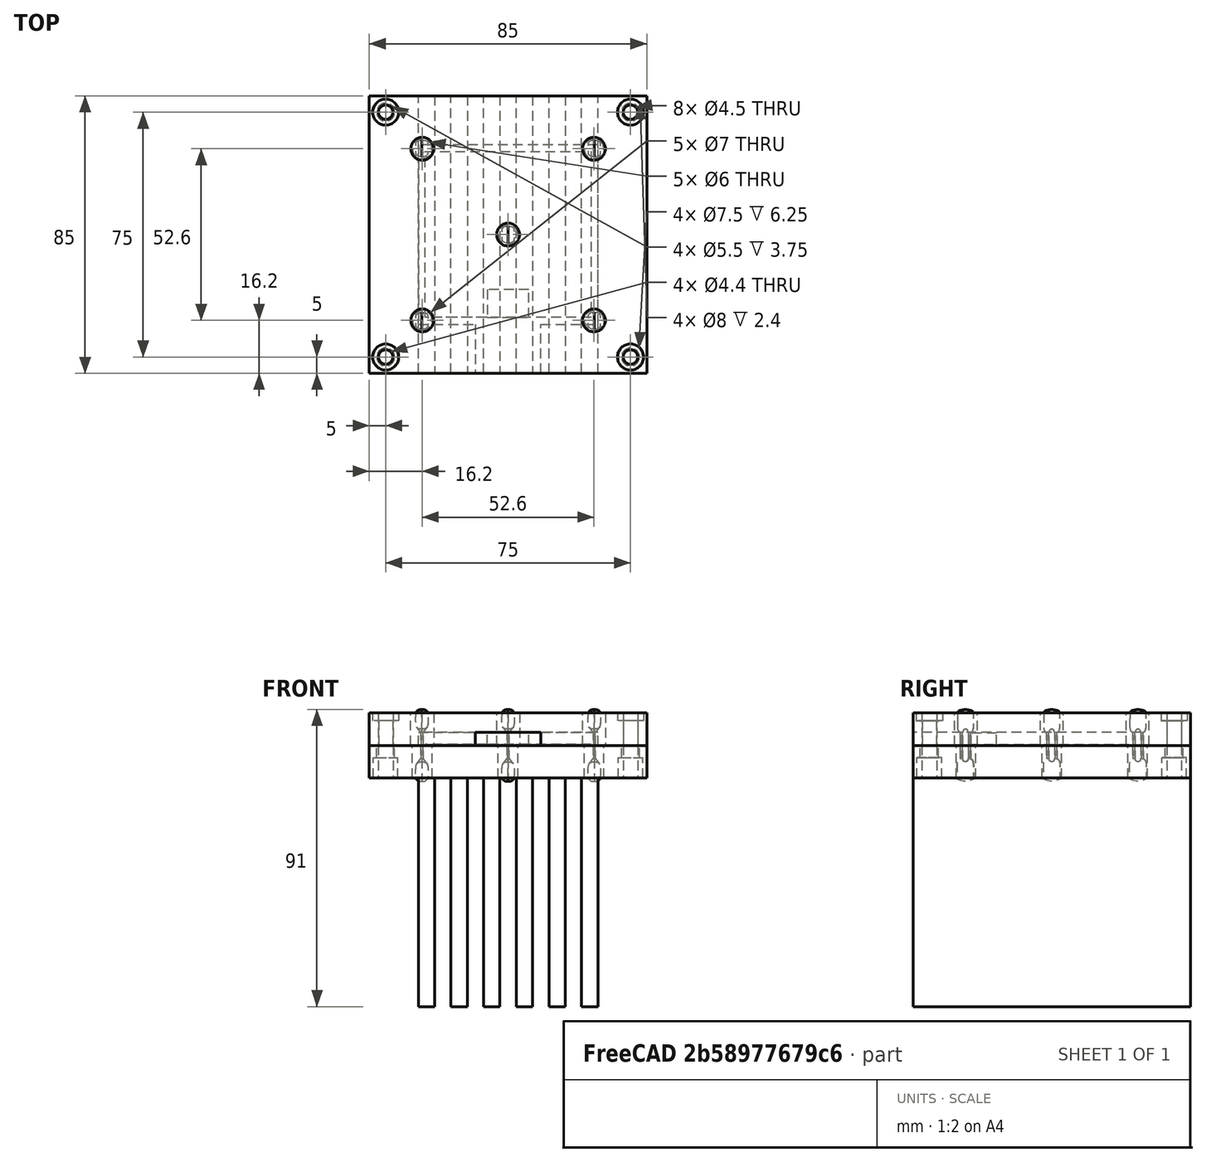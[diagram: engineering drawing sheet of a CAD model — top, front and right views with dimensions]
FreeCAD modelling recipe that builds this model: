
FCSTD DOCUMENT  (FreeCAD 0.18R4 (GitTag))
Label: thermal_cond_tester
License: All rights reserved
LicenseURL: http://en.wikipedia.org/wiki/All_rights_reserved
objects: PartDesign::Body×16, Sketcher::SketchObject×15, PartDesign::FeatureBase×11, PartDesign::Pad×6, PartDesign::Pocket×6, PartDesign::Hole×5, PartDesign::Mirrored×2, App::DocumentObjectGroup×2, App::Part×2, Part::Feature×1, Spreadsheet::Sheet×1, Fem::FemSolverObjectPython×1
note: 79 computed .brp shape members not serialized (recipe doc carries the construction recipe); baked Part::Feature solids carry a one-line shape summary decoded from their .brp

FEATURE [Sketcher::SketchObject] Sketch
  MapMode = 5
  Support = -> [XY_Plane003]
  sketch-geometry (4):
    g0: LineSegment StartX=-42.5 StartY=42.5 StartZ=0 EndX=42.5 EndY=42.5 EndZ=0
    g1: LineSegment StartX=42.5 StartY=42.5 StartZ=0 EndX=42.5 EndY=-42.5 EndZ=0
    g2: LineSegment StartX=42.5 StartY=-42.5 StartZ=0 EndX=-42.5 EndY=-42.5 EndZ=0
    g3: LineSegment StartX=-42.5 StartY=-42.5 StartZ=0 EndX=-42.5 EndY=42.5 EndZ=0
  constraints (12):
    c: Coincident(g0,g1)
    c: Coincident(g1,g2)
    c: Coincident(g2,g3)
    c: Coincident(g3,g0)
    c: Horizontal(g0)
    c: Horizontal(g2)
    c: Vertical(g1)
    c: Vertical(g3)
    c: DistanceX(g0,g0) = 85
    c: DistanceY(g1,g1) = 85
    c: DistanceX(g2,g-1) = 42.5
    c: DistanceY(g2,g-1) = 42.5
FEATURE [Sketcher::SketchObject] Sketch003
  MapMode = 2
  sketch-geometry (4):
    g0: LineSegment StartX=-25.4 StartY=25.4 StartZ=0 EndX=25.4 EndY=25.4 EndZ=0
    g1: LineSegment StartX=25.4 StartY=25.4 StartZ=0 EndX=25.4 EndY=-25.4 EndZ=0
    g2: LineSegment StartX=25.4 StartY=-25.4 StartZ=0 EndX=-25.4 EndY=-25.4 EndZ=0
    g3: LineSegment StartX=-25.4 StartY=-25.4 StartZ=0 EndX=-25.4 EndY=25.4 EndZ=0
  constraints (10):
    c: Coincident(g0,g1)
    c: Coincident(g1,g2)
    c: Coincident(g2,g3)
    c: Coincident(g3,g0)
    c: Horizontal(g2)
    c: Vertical(g1)
    c: Symmetric(g0,g0,g-2)
    c: Symmetric(g2,g0,g-1)
    c: DistanceX(g0,g0) = 50.8
    c: DistanceY(g1,g1) = 50.8
FEATURE [PartDesign::Pad] Pad001
  Length = 0.3
  Length2 = 100
  Profile = -> Sketch003
  Type = 0
FEATURE [Sketcher::SketchObject] Sketch004
  ExternalGeometry = -> [Pad001]
  MapMode = 5
  Placement = pos=(0,0,0.3) rot=(0,0,1;0rad)
  Support = -> [Pad001]
  sketch-geometry (4):
    g0: LineSegment StartX=6.35 StartY=-16.9 StartZ=0 EndX=-6.35 EndY=-16.9 EndZ=0
    g1: LineSegment StartX=-6.35 StartY=-16.9 StartZ=0 EndX=-6.35 EndY=-25.4 EndZ=0
    g2: LineSegment StartX=-6.35 StartY=-25.4 StartZ=0 EndX=6.35 EndY=-25.4 EndZ=0
    g3: LineSegment StartX=6.35 StartY=-25.4 StartZ=0 EndX=6.35 EndY=-16.9 EndZ=0
  constraints (11):
    c: Coincident(g0,g1)
    c: Coincident(g1,g2)
    c: Coincident(g2,g3)
    c: Coincident(g3,g0)
    c: Horizontal(g2)
    c: Vertical(g1)
    c: Vertical(g3)
    c: PointOnObject(g2,g-3)
    c: Symmetric(g0,g0,g-2)
    c: DistanceX(g0,g0) = 12.7
    c: DistanceY(g1,g1) = 8.5
FEATURE [PartDesign::Pad] Pad002
  BaseFeature = -> Pad001
  Length = 3.51
  Length2 = 100
  Profile = -> Sketch004
  Type = 0
FEATURE [PartDesign::Body] Body001  label="Heater Foil"
  Group = -> [Sketch003,Pad001,Sketch004,Pad002]
  Origin = -> Origin001
  Tip = -> Pad002
FEATURE [PartDesign::Pad] Pad
  Length = 10
  Length2 = 100
  Profile = -> Sketch
  Type = 0
FEATURE [Sketcher::SketchObject] Sketch002
  ExternalGeometry = -> [Pad]
  MapMode = 5
  Placement = pos=(0,0,10) rot=(0,0,1;0rad)
  Support = -> [Pad]
  sketch-geometry (4):
    g0: Circle CenterX=-37.5 CenterY=37.5 CenterZ=0 NormalX=0 NormalY=0 NormalZ=1 AngleXU=0 Radius=2
    g1: Circle CenterX=37.5 CenterY=37.5 CenterZ=0 NormalX=0 NormalY=0 NormalZ=1 AngleXU=0 Radius=2
    g2: Circle CenterX=37.5 CenterY=-37.5 CenterZ=0 NormalX=0 NormalY=0 NormalZ=1 AngleXU=0 Radius=2
    g3: Circle CenterX=-37.5 CenterY=-37.5 CenterZ=0 NormalX=0 NormalY=0 NormalZ=1 AngleXU=0 Radius=2
  constraints (9):
    c: Symmetric(g1,g0,g-2)
    c: Symmetric(g2,g1,g-1)
    c: Symmetric(g0,g3,g-1)
    c: DistanceX(g-3,g0) = 5
    c: DistanceY(g0,g-3) = 5
    c: Radius(g0) = 2
    c: Equal(g0,g1)
    c: Equal(g1,g2)
    c: Equal(g2,g3)
FEATURE [PartDesign::Hole] Hole
  BaseFeature = -> Pad
  Depth = 25
  DepthType = 0
  Diameter = 4.4
  DrillPoint = 1
  DrillPointAngle = 118
  HoleCutCountersinkAngle = 90
  HoleCutDepth = 2.4
  HoleCutDiameter = 8
  HoleCutType = 1
  ModelActualThread = false
  Profile = -> Sketch002
  Tapered = false
  TaperedAngle = 90
  ThreadAngle = 60
  ThreadClass = 0
  ThreadCutOffInner = 0.0541266
  ThreadCutOffOuter = 0.108253
  ThreadDirection = 0
  ThreadFit = 0
  ThreadPitch = 0.5
  ThreadSize = 11
  ThreadType = 2
  Threaded = false
FEATURE [Sketcher::SketchObject] Sketch001
  MapMode = 5
  Placement = pos=(0,0,0) rot=(1,0,0;3.14159rad)
  Support = -> [Pad]
  sketch-geometry (4):
    g0: LineSegment StartX=-27.5 StartY=27.5 StartZ=0 EndX=27.5 EndY=27.5 EndZ=0
    g1: LineSegment StartX=27.5 StartY=27.5 StartZ=0 EndX=27.5 EndY=-27.5 EndZ=0
    g2: LineSegment StartX=27.5 StartY=-27.5 StartZ=0 EndX=-27.5 EndY=-27.5 EndZ=0
    g3: LineSegment StartX=-27.5 StartY=-27.5 StartZ=0 EndX=-27.5 EndY=27.5 EndZ=0
  constraints (10):
    c: Coincident(g0,g1)
    c: Coincident(g1,g2)
    c: Coincident(g2,g3)
    c: Coincident(g3,g0)
    c: Horizontal(g2)
    c: Vertical(g3)
    c: Symmetric(g0,g0,g-2)
    c: Symmetric(g1,g0,g-1)
    c: DistanceX(g0,g0) = 55
    c: Equal(g1,g0)
FEATURE [PartDesign::Pocket] Pocket
  BaseFeature = -> Hole
  Length = 4
  Length2 = 100
  Profile = -> Sketch001
  Type = 0
FEATURE [PartDesign::Pad] Pad003
  Length = 10
  Length2 = 100
  Profile = -> Sketch
  Type = 0
FEATURE [Sketcher::SketchObject] Sketch005
  ExternalGeometry = -> [Pad]
  MapMode = 5
  Placement = pos=(0,0,10) rot=(0,0,1;0rad)
  Support = -> [Pad]
  sketch-geometry (4):
    g0: Circle CenterX=-37.5 CenterY=37.5 CenterZ=0 NormalX=0 NormalY=0 NormalZ=1 AngleXU=0 Radius=2
    g1: Circle CenterX=37.5 CenterY=37.5 CenterZ=0 NormalX=0 NormalY=0 NormalZ=1 AngleXU=0 Radius=2
    g2: Circle CenterX=37.5 CenterY=-37.5 CenterZ=0 NormalX=0 NormalY=0 NormalZ=1 AngleXU=0 Radius=2
    g3: Circle CenterX=-37.5 CenterY=-37.5 CenterZ=0 NormalX=0 NormalY=0 NormalZ=1 AngleXU=0 Radius=2
  constraints (9):
    c: Symmetric(g1,g0,g-2)
    c: Symmetric(g2,g1,g-1)
    c: Symmetric(g0,g3,g-1)
    c: DistanceX(g-3,g0) = 5
    c: DistanceY(g0,g-3) = 5
    c: Radius(g0) = 2
    c: Equal(g0,g1)
    c: Equal(g1,g2)
    c: Equal(g2,g3)
FEATURE [PartDesign::Hole] Hole001
  BaseFeature = -> Pad003
  Depth = 25
  DepthType = 0
  Diameter = 4.5
  DrillPoint = 1
  DrillPointAngle = 118
  HoleCutCountersinkAngle = 90
  HoleCutDepth = 0
  HoleCutDiameter = 5
  HoleCutType = 0
  ModelActualThread = false
  Profile = -> Sketch005
  Tapered = false
  TaperedAngle = 90
  ThreadAngle = 60
  ThreadClass = 0
  ThreadCutOffInner = 0.0541266
  ThreadCutOffOuter = 0.108253
  ThreadDirection = 1
  ThreadFit = 0
  ThreadPitch = 0.5
  ThreadSize = 13
  ThreadType = 2
  Threaded = true
FEATURE [Part::Feature] Part__Feature  label="Thermister Ref"
  Placement = pos=(26.3,26.3,-4) rot=(0,1,0;1.5708rad)
  shape: bbox 4.003 x 5.103 x 24 mm, 8 faces (baked)
FEATURE [Sketcher::SketchObject] Sketch006
  MapMode = 5
  Placement = pos=(0,0,0) rot=(1,0,0;3.14159rad)
  Support = -> [Hole001]
  sketch-geometry (5):
    g0: Circle CenterX=0 CenterY=0 CenterZ=0 NormalX=0 NormalY=0 NormalZ=1 AngleXU=0 Radius=3.5
    g1: Circle CenterX=-26.3 CenterY=26.3 CenterZ=0 NormalX=0 NormalY=0 NormalZ=1 AngleXU=0 Radius=3.5
    g2: Circle CenterX=26.3 CenterY=26.3 CenterZ=0 NormalX=0 NormalY=0 NormalZ=1 AngleXU=0 Radius=3.5
    g3: Circle CenterX=26.3 CenterY=-26.3 CenterZ=0 NormalX=0 NormalY=0 NormalZ=1 AngleXU=0 Radius=3.5
    g4: Circle CenterX=-26.3 CenterY=-26.3 CenterZ=0 NormalX=0 NormalY=0 NormalZ=1 AngleXU=0 Radius=3.5
  constraints (11):
    c: Diameter(g0) = 7
    c: Coincident(g0,g-1)
    c: Equal(g4,g1)
    c: Equal(g1,g0)
    c: Equal(g0,g2)
    c: Equal(g2,g3)
    c: Symmetric(g1,g2,g-2)
    c: Symmetric(g2,g3,g-1)
    c: Symmetric(g4,g1,g-1)
    c: DistanceX(g1,g-1) = 26.3
    c: DistanceY(g-1,g1) = 26.3
FEATURE [PartDesign::Hole] Hole002
  BaseFeature = -> Hole001
  Depth = 25
  DepthType = 0
  Diameter = 6
  DrillPoint = 1
  DrillPointAngle = 118
  HoleCutCountersinkAngle = 90
  HoleCutDepth = 0
  HoleCutDiameter = 0
  HoleCutType = 0
  ModelActualThread = false
  Profile = -> Sketch006
  Tapered = false
  TaperedAngle = 90
  ThreadAngle = 0
  ThreadClass = 0
  ThreadCutOffInner = 0
  ThreadCutOffOuter = 0
  ThreadDirection = 0
  ThreadFit = 0
  ThreadPitch = 0
  ThreadSize = 0
  ThreadType = 0
  Threaded = false
FEATURE [PartDesign::Body] Body002  label="Hot Plate Bottom"
  Group = -> [Pad003,Sketch005,Hole001,Sketch006,Hole002]
  Origin = -> Origin003
  Placement = pos=(0,0,-10) rot=(0,0,1;0rad)
  Tip = -> Hole002
FEATURE [Spreadsheet::Sheet] Spreadsheet
  cells = B3=Part Desc; C3=URL; B4=Thermistor; C4=https://www.digikey.com/product-detail/en/vishay-bc-components/NTCLE100E3103JB0/BC2301-ND/769411; B5=Heater; C5=http://catalog.minco.com/catalog3/d/minco/?c=products&cid=3_1-polyimide-thermofoil-heaters&id=HK6911
FEATURE [PartDesign::FeatureBase] BaseFeature
  BaseFeature = -> Part__Feature
FEATURE [PartDesign::Pocket] Pocket001
  BaseFeature = -> BaseFeature
  Length = 10
  Length2 = 100
  Profile = -> BaseFeature [Face6]
  Type = 0
FEATURE [PartDesign::Mirrored] Mirrored
  BaseFeature = -> Pocket001
  MirrorPlane = -> XZ_Plane004
  Originals = -> [Pocket001]
FEATURE [PartDesign::Body] Body003  label="Shortened Thermister"
  BaseFeature = -> Part__Feature
  Group = -> [BaseFeature,Pocket001,Mirrored]
  Origin = -> Origin004
  Tip = -> Mirrored
FEATURE [PartDesign::FeatureBase] Clone
  BaseFeature = -> Body003
FEATURE [PartDesign::Body] Body004  label="Thermister 1"
  BaseFeature = -> Body003
  Group = -> [Clone]
  Origin = -> Origin005
  Placement = pos=(0,0,-4) rot=(0,1,0;1.5708rad)
  Tip = -> Clone
FEATURE [PartDesign::FeatureBase] Clone001
  BaseFeature = -> Body003
FEATURE [PartDesign::Body] Body005  label="Thermister 2"
  BaseFeature = -> Body003
  Group = -> [Clone001]
  Origin = -> Origin006
  Placement = pos=(26.4,26.4,-4) rot=(0,1,0;1.5708rad)
  Tip = -> Clone001
FEATURE [PartDesign::FeatureBase] Clone002
  BaseFeature = -> Body003
FEATURE [PartDesign::Body] Body006  label="Thermister 3"
  BaseFeature = -> Body003
  Group = -> [Clone002]
  Origin = -> Origin007
  Placement = pos=(26.4,-26.4,-4) rot=(0,1,0;1.5708rad)
  Tip = -> Clone002
FEATURE [PartDesign::FeatureBase] Clone003
  BaseFeature = -> Body003
FEATURE [PartDesign::Body] Body007  label="Thermister 4"
  BaseFeature = -> Body003
  Group = -> [Clone003]
  Origin = -> Origin008
  Placement = pos=(-26.4,26.4,-4) rot=(0,1,0;1.5708rad)
  Tip = -> Clone003
FEATURE [PartDesign::FeatureBase] Clone004
  BaseFeature = -> Body003
FEATURE [PartDesign::Body] Body008  label="Thermister 5"
  BaseFeature = -> Body003
  Group = -> [Clone004]
  Origin = -> Origin009
  Placement = pos=(-26.4,-26.5,-4) rot=(0,1,0;1.5708rad)
  Tip = -> Clone004
FEATURE [App::DocumentObjectGroup] Group  label="Reference Parts"
  Group = -> [Part__Feature,Body003]
FEATURE [App::DocumentObjectGroup] Group001  label="Documentation"
  Group = -> [Spreadsheet]
FEATURE [Sketcher::SketchObject] Sketch007
  ExternalGeometry = -> [Pocket]
  MapMode = 5
  Placement = pos=(0,0,0) rot=(1,0,0;3.14159rad)
  Support = -> [Pocket]
  sketch-geometry (4):
    g0: LineSegment StartX=-10 StartY=42.5 StartZ=0 EndX=10 EndY=42.5 EndZ=0
    g1: LineSegment StartX=10 StartY=42.5 StartZ=0 EndX=10 EndY=27.5 EndZ=0
    g2: LineSegment StartX=10 StartY=27.5 StartZ=0 EndX=-10 EndY=27.5 EndZ=0
    g3: LineSegment StartX=-10 StartY=27.5 StartZ=0 EndX=-10 EndY=42.5 EndZ=0
  constraints (11):
    c: Coincident(g0,g1)
    c: Coincident(g1,g2)
    c: Coincident(g2,g3)
    c: Coincident(g3,g0)
    c: Horizontal(g0)
    c: Vertical(g1)
    c: Vertical(g3)
    c: PointOnObject(g0,g-3)
    c: PointOnObject(g2,g-4)
    c: Symmetric(g2,g1,g-2)
    c: DistanceX(g2,g2) = 20
FEATURE [PartDesign::Pocket] Pocket002
  BaseFeature = -> Pocket
  Length = 4
  Length2 = 100
  Profile = -> Sketch007
  Type = 0
FEATURE [PartDesign::Body] Body  label="Hot Plate Top"
  Group = -> [Sketch,Pad,Sketch001,Sketch002,Hole,Pocket,Sketch007,Pocket002]
  Origin = -> Origin
  Tip = -> Pocket002
FEATURE [App::Part] Part  label="Hot Side"
  Group = -> [Body001,Body,Body002,Body004,Body005,Body006,Body007,Body008]
  Origin = -> Origin002
FEATURE [Sketcher::SketchObject] Sketch008
  MapMode = 5
  Support = -> [XY_Plane011]
  sketch-geometry (4):
    g0: LineSegment StartX=-42.5 StartY=42.5 StartZ=0 EndX=42.5 EndY=42.5 EndZ=0
    g1: LineSegment StartX=42.5 StartY=42.5 StartZ=0 EndX=42.5 EndY=-42.5 EndZ=0
    g2: LineSegment StartX=42.5 StartY=-42.5 StartZ=0 EndX=-42.5 EndY=-42.5 EndZ=0
    g3: LineSegment StartX=-42.5 StartY=-42.5 StartZ=0 EndX=-42.5 EndY=42.5 EndZ=0
  constraints (10):
    c: Coincident(g0,g1)
    c: Coincident(g1,g2)
    c: Coincident(g2,g3)
    c: Coincident(g3,g0)
    c: Horizontal(g2)
    c: Vertical(g3)
    c: DistanceX(g0,g0) = 85
    c: Symmetric(g0,g0,g-2)
    c: Equal(g1,g0)
    c: Symmetric(g1,g0,g-1)
FEATURE [PartDesign::Pad] Pad004
  Length = 10
  Length2 = 100
  Profile = -> Sketch008
  Type = 0
FEATURE [Sketcher::SketchObject] Sketch009
  ExternalGeometry = -> [Pad004]
  MapMode = 5
  Placement = pos=(0,0,10) rot=(0,0,1;0rad)
  Support = -> [Pad004]
  sketch-geometry (4):
    g0: Circle CenterX=-37.5 CenterY=37.5 CenterZ=0 NormalX=0 NormalY=0 NormalZ=1 AngleXU=0 Radius=2
    g1: Circle CenterX=37.5 CenterY=37.5 CenterZ=0 NormalX=0 NormalY=0 NormalZ=1 AngleXU=0 Radius=2
    g2: Circle CenterX=37.5 CenterY=-37.5 CenterZ=0 NormalX=0 NormalY=0 NormalZ=1 AngleXU=0 Radius=2
    g3: Circle CenterX=-37.5 CenterY=-37.5 CenterZ=0 NormalX=0 NormalY=0 NormalZ=1 AngleXU=0 Radius=2
  constraints (9):
    c: Radius(g0) = 2
    c: DistanceX(g-3,g0) = 5
    c: DistanceY(g0,g-3) = 5
    c: Equal(g0,g1)
    c: Equal(g1,g2)
    c: Equal(g2,g3)
    c: Symmetric(g0,g1,g-2)
    c: Symmetric(g3,g2,g-2)
    c: Symmetric(g0,g3,g-1)
FEATURE [PartDesign::Hole] Hole003
  BaseFeature = -> Pad004
  Depth = 25
  DepthType = 0
  Diameter = 4.5
  DrillPoint = 1
  DrillPointAngle = 118
  HoleCutCountersinkAngle = 90
  HoleCutDepth = 0
  HoleCutDiameter = 5
  HoleCutType = 0
  ModelActualThread = false
  Profile = -> Sketch009
  Tapered = false
  TaperedAngle = 90
  ThreadAngle = 60
  ThreadClass = 0
  ThreadCutOffInner = 0.0541266
  ThreadCutOffOuter = 0.108253
  ThreadDirection = 1
  ThreadFit = 0
  ThreadPitch = 0.5
  ThreadSize = 13
  ThreadType = 2
  Threaded = true
FEATURE [Sketcher::SketchObject] Sketch010
  MapMode = 5
  Placement = pos=(0,0,10) rot=(0,0,1;0rad)
  Support = -> [Hole003]
  sketch-geometry (5):
    g0: Circle CenterX=0 CenterY=0 CenterZ=0 NormalX=0 NormalY=0 NormalZ=1 AngleXU=0 Radius=3.5
    g1: Circle CenterX=-26.3 CenterY=26.3 CenterZ=0 NormalX=0 NormalY=0 NormalZ=1 AngleXU=0 Radius=3.5
    g2: Circle CenterX=26.3 CenterY=26.3 CenterZ=0 NormalX=0 NormalY=0 NormalZ=1 AngleXU=0 Radius=3.5
    g3: Circle CenterX=26.3 CenterY=-26.3 CenterZ=0 NormalX=0 NormalY=0 NormalZ=1 AngleXU=0 Radius=3.5
    g4: Circle CenterX=-26.3 CenterY=-26.3 CenterZ=0 NormalX=0 NormalY=0 NormalZ=1 AngleXU=0 Radius=3.5
  constraints (11):
    c: Diameter(g0) = 7
    c: Coincident(g0,g-1)
    c: Equal(g1,g0)
    c: Equal(g0,g2)
    c: Equal(g2,g3)
    c: Equal(g3,g4)
    c: DistanceX(g1,g0) = 26.3
    c: Symmetric(g1,g2,g-2)
    c: Symmetric(g4,g1,g-1)
    c: Symmetric(g3,g2,g-1)
    c: DistanceY(g0,g1) = 26.3
FEATURE [PartDesign::Pocket] Pocket003
  BaseFeature = -> Hole003
  Length = 10
  Length2 = 100
  Profile = -> Sketch010
  Type = 0
FEATURE [PartDesign::Body] Body009  label="Cold Plate Top"
  Group = -> [Sketch008,Pad004,Sketch009,Hole003,Sketch010,Pocket003]
  Origin = -> Origin011
  Tip = -> Pocket003
FEATURE [PartDesign::FeatureBase] Clone005
  BaseFeature = -> Body003
FEATURE [PartDesign::Body] Body010  label="Thermistor 6"
  BaseFeature = -> Body003
  Group = -> [Clone005]
  Origin = -> Origin012
  Placement = pos=(0,0,4) rot=(0,-1,0;1.5708rad)
  Tip = -> Clone005
FEATURE [PartDesign::FeatureBase] Clone006
  BaseFeature = -> Body003
FEATURE [PartDesign::Body] Body011  label="Thermistor 7"
  BaseFeature = -> Body003
  Group = -> [Clone006]
  Origin = -> Origin013
  Placement = pos=(26.4,26.4,4) rot=(0,-1,0;1.5708rad)
  Tip = -> Clone006
FEATURE [PartDesign::FeatureBase] Clone007
  BaseFeature = -> Body003
FEATURE [PartDesign::Body] Body012  label="Thermistor 8"
  BaseFeature = -> Body003
  Group = -> [Clone007]
  Origin = -> Origin014
  Placement = pos=(26.4,-26.4,4) rot=(0,-1,0;1.5708rad)
  Tip = -> Clone007
FEATURE [PartDesign::FeatureBase] Clone008
  BaseFeature = -> Body003
FEATURE [PartDesign::Body] Body013  label="Thermistor 9"
  BaseFeature = -> Body003
  Group = -> [Clone008]
  Origin = -> Origin015
  Placement = pos=(-26.4,26.4,4) rot=(0,-1,0;1.5708rad)
  Tip = -> Clone008
FEATURE [PartDesign::FeatureBase] Clone009
  BaseFeature = -> Body003
FEATURE [PartDesign::Body] Body014  label="Thermistor 10"
  BaseFeature = -> Body003
  Group = -> [Clone009]
  Origin = -> Origin016
  Placement = pos=(-26.4,-26.4,4) rot=(0,-1,0;1.5708rad)
  Tip = -> Clone009
FEATURE [Sketcher::SketchObject] Sketch011
  MapMode = 5
  Support = -> [XY_Plane017]
  sketch-geometry (4):
    g0: LineSegment StartX=-42.5 StartY=42.5 StartZ=0 EndX=42.5 EndY=42.5 EndZ=0
    g1: LineSegment StartX=42.5 StartY=42.5 StartZ=0 EndX=42.5 EndY=-42.5 EndZ=0
    g2: LineSegment StartX=42.5 StartY=-42.5 StartZ=0 EndX=-42.5 EndY=-42.5 EndZ=0
    g3: LineSegment StartX=-42.5 StartY=-42.5 StartZ=0 EndX=-42.5 EndY=42.5 EndZ=0
  constraints (10):
    c: Coincident(g0,g1)
    c: Coincident(g1,g2)
    c: Coincident(g2,g3)
    c: Coincident(g3,g0)
    c: Horizontal(g2)
    c: Vertical(g3)
    c: DistanceX(g0,g0) = 85
    c: Symmetric(g0,g0,g-2)
    c: Equal(g1,g0)
    c: Symmetric(g1,g0,g-1)
FEATURE [PartDesign::Pad] Pad005
  Length = 80
  Length2 = 100
  Profile = -> Sketch011
  Type = 0
FEATURE [Sketcher::SketchObject] Sketch012
  ExternalGeometry = -> [Pad005]
  MapMode = 5
  Placement = pos=(0,0,0) rot=(1,0,0;3.14159rad)
  Support = -> [Pad005]
  sketch-geometry (4):
    g0: LineSegment StartX=27.5 StartY=-42.5 StartZ=0 EndX=42.5 EndY=-42.5 EndZ=0
    g1: LineSegment StartX=42.5 StartY=-42.5 StartZ=0 EndX=42.5 EndY=42.5 EndZ=0
    g2: LineSegment StartX=42.5 StartY=42.5 StartZ=0 EndX=27.5 EndY=42.5 EndZ=0
    g3: LineSegment StartX=27.5 StartY=42.5 StartZ=0 EndX=27.5 EndY=-42.5 EndZ=0
  constraints (10):
    c: Coincident(g0,g1)
    c: Coincident(g1,g2)
    c: Coincident(g2,g3)
    c: Coincident(g3,g0)
    c: Horizontal(g0)
    c: Horizontal(g2)
    c: Vertical(g3)
    c: Coincident(g0,g-4)
    c: Coincident(g1,g-3)
    c: DistanceX(g2,g2) = 15
FEATURE [PartDesign::Pocket] Pocket004
  BaseFeature = -> Pad005
  Length = 70
  Length2 = 100
  Profile = -> Sketch012
  Type = 0
FEATURE [PartDesign::Mirrored] Mirrored001
  BaseFeature = -> Pocket004
  MirrorPlane = -> Sketch012 [V_Axis]
  Originals = -> [Pocket004]
FEATURE [Sketcher::SketchObject] Sketch013
  ExternalGeometry = -> [Mirrored001]
  MapMode = 5
  Placement = pos=(0,0,70) rot=(1,0,0;3.14159rad)
  Support = -> [Mirrored001]
  sketch-geometry (4):
    g0: Circle CenterX=-37.5 CenterY=37.5 CenterZ=0 NormalX=0 NormalY=0 NormalZ=1 AngleXU=0 Radius=2
    g1: Circle CenterX=37.5 CenterY=37.5 CenterZ=0 NormalX=0 NormalY=0 NormalZ=1 AngleXU=0 Radius=2
    g2: Circle CenterX=37.5 CenterY=-37.5 CenterZ=0 NormalX=0 NormalY=0 NormalZ=1 AngleXU=0 Radius=2
    g3: Circle CenterX=-37.5 CenterY=-37.5 CenterZ=0 NormalX=0 NormalY=0 NormalZ=1 AngleXU=0 Radius=2
  constraints (9):
    c: Equal(g3,g0)
    c: Equal(g0,g1)
    c: Equal(g1,g2)
    c: Symmetric(g1,g0,g-2)
    c: Symmetric(g0,g3,g-1)
    c: Symmetric(g2,g1,g-1)
    c: DistanceX(g-3,g0) = 5
    c: DistanceY(g0,g-3) = 5
    c: Radius(g0) = 2
FEATURE [PartDesign::Hole] Hole004
  BaseFeature = -> Mirrored001
  Depth = 25
  DepthType = 0
  Diameter = 5.5
  DrillPoint = 1
  DrillPointAngle = 118
  HoleCutCountersinkAngle = 90
  HoleCutDepth = 6.25
  HoleCutDiameter = 7.5
  HoleCutType = -1
  ModelActualThread = false
  Profile = -> Sketch013
  Tapered = false
  TaperedAngle = 90
  ThreadAngle = 0
  ThreadClass = 0
  ThreadCutOffInner = 0
  ThreadCutOffOuter = 0
  ThreadDirection = 0
  ThreadFit = 0
  ThreadPitch = 0
  ThreadSize = -1
  ThreadType = 2
  Threaded = false
FEATURE [Sketcher::SketchObject] Sketch014
  ExternalGeometry = -> [Hole004]
  MapMode = 5
  Placement = pos=(0,0,0) rot=(1,0,0;3.14159rad)
  Support = -> [Hole004]
  sketch-geometry (20):
    g0: LineSegment StartX=-22.5 StartY=42.5 StartZ=0 EndX=-17.5 EndY=42.5 EndZ=0
    g1: LineSegment StartX=-17.5 StartY=42.5 StartZ=0 EndX=-17.5 EndY=-42.5 EndZ=0
    g2: LineSegment StartX=-17.5 StartY=-42.5 StartZ=0 EndX=-22.5 EndY=-42.5 EndZ=0
    g3: LineSegment StartX=-22.5 StartY=-42.5 StartZ=0 EndX=-22.5 EndY=42.5 EndZ=0
    g4: LineSegment StartX=-12.5 StartY=42.5 StartZ=0 EndX=-7.5 EndY=42.5 EndZ=0
    g5: LineSegment StartX=-7.5 StartY=42.5 StartZ=0 EndX=-7.5 EndY=-42.5 EndZ=0
    g6: LineSegment StartX=-7.5 StartY=-42.5 StartZ=0 EndX=-12.5 EndY=-42.5 EndZ=0
    g7: LineSegment StartX=-12.5 StartY=-42.5 StartZ=0 EndX=-12.5 EndY=42.5 EndZ=0
    g8: LineSegment StartX=-2.5 StartY=42.5 StartZ=0 EndX=2.5 EndY=42.5 EndZ=0
    g9: LineSegment StartX=2.5 StartY=42.5 StartZ=0 EndX=2.5 EndY=-42.5 EndZ=0
    g10: LineSegment StartX=2.5 StartY=-42.5 StartZ=0 EndX=-2.5 EndY=-42.5 EndZ=0
    g11: LineSegment StartX=-2.5 StartY=-42.5 StartZ=0 EndX=-2.5 EndY=42.5 EndZ=0
    g12: LineSegment StartX=7.5 StartY=42.5 StartZ=0 EndX=12.5 EndY=42.5 EndZ=0
    g13: LineSegment StartX=12.5 StartY=42.5 StartZ=0 EndX=12.5 EndY=-42.5 EndZ=0
    g14: LineSegment StartX=12.5 StartY=-42.5 StartZ=0 EndX=7.5 EndY=-42.5 EndZ=0
    g15: LineSegment StartX=7.5 StartY=-42.5 StartZ=0 EndX=7.5 EndY=42.5 EndZ=0
    g16: LineSegment StartX=17.5 StartY=42.5 StartZ=0 EndX=22.5 EndY=42.5 EndZ=0
    g17: LineSegment StartX=22.5 StartY=42.5 StartZ=0 EndX=22.5 EndY=-42.5 EndZ=0
    g18: LineSegment StartX=22.5 StartY=-42.5 StartZ=0 EndX=17.5 EndY=-42.5 EndZ=0
    g19: LineSegment StartX=17.5 StartY=-42.5 StartZ=0 EndX=17.5 EndY=42.5 EndZ=0
  constraints (61):
    c: Coincident(g0,g1)
    c: Coincident(g1,g2)
    c: Coincident(g2,g3)
    c: Coincident(g3,g0)
    c: Horizontal(g0)
    c: Horizontal(g2)
    c: Vertical(g1)
    c: Vertical(g3)
    c: PointOnObject(g0,g-3)
    c: PointOnObject(g2,g-4)
    c: DistanceX(g-4,g-4) = 55
    c: DistanceX(g2,g2) = 5
    c: DistanceX(g-4,g2) = 5
    c: Coincident(g4,g5)
    c: Coincident(g5,g6)
    c: Coincident(g6,g7)
    c: Coincident(g7,g4)
    c: Horizontal(g4)
    c: Horizontal(g6)
    c: Vertical(g5)
    c: Vertical(g7)
    c: Coincident(g8,g9)
    c: Coincident(g9,g10)
    c: Coincident(g10,g11)
    c: Coincident(g11,g8)
    c: Horizontal(g8)
    c: Horizontal(g10)
    c: Vertical(g9)
    c: Vertical(g11)
    c: Coincident(g12,g13)
    c: Coincident(g13,g14)
    c: Coincident(g14,g15)
    c: Coincident(g15,g12)
    c: Horizontal(g12)
    c: Horizontal(g14)
    c: Vertical(g13)
    c: Vertical(g15)
    c: Coincident(g16,g17)
    c: Coincident(g17,g18)
    c: Coincident(g18,g19)
    c: Coincident(g19,g16)
    c: Horizontal(g16)
    c: Horizontal(g18)
    c: Vertical(g17)
    c: Vertical(g19)
    c: Equal(g2,g6)
    c: Equal(g6,g10)
    c: Equal(g10,g14)
    c: Equal(g14,g18)
    c: Equal(g3,g7)
    c: Equal(g7,g11)
    c: Equal(g11,g15)
    c: Equal(g15,g19)
    c: Horizontal(g2,g6)
    c: Horizontal(g6,g10)
    c: Horizontal(g10,g14)
    c: Horizontal(g14,g18)
    c: DistanceX(g-4,g6) = 15
    c: DistanceX(g-4,g10) = 25
    c: DistanceX(g-4,g14) = 35
    c: DistanceX(g-4,g18) = 45
FEATURE [PartDesign::Pocket] Pocket005
  BaseFeature = -> Hole004
  Length = 70
  Length2 = 100
  Profile = -> Sketch014
  Type = 0
FEATURE [PartDesign::Body] Body015  label="Cold Plate Bottom"
  Group = -> [Pad005,Sketch011,Sketch012,Pocket004,Mirrored001,Sketch013,Hole004,Sketch014,Pocket005]
  Origin = -> Origin017
  Placement = pos=(0,0,-80) rot=(0,0,1;0rad)
  Tip = -> Pocket005
FEATURE [App::Part] Part001  label="Cold Side"
  Group = -> [Body009,Body010,Body011,Body012,Body013,Body014,Body015]
  Origin = -> Origin010
  Placement = pos=(0,0,-24) rot=(0,0,1;0rad)
FEATURE [Fem::FemSolverObjectPython] CalculiXccxTools  # FEM object (typed FeaturePython)
  AnalysisType = 0
  BeamShellResultOutput3D = false
  EigenmodeHighLimit = 1000000
  EigenmodeLowLimit = 0
  EigenmodesCount = 10
  GeometricalNonlinearity = 0
  IterationsControlParameterCutb = 0.25,0.5,0.75,0.85,,,1.5,
  IterationsControlParameterIter = 4,8,9,200,10,400,,200,,
  IterationsControlParameterTimeUse = false
  IterationsThermoMechMaximum = 200
  IterationsUserDefinedIncrementations = false
  IterationsUserDefinedTimeStepLength = false
  MaterialNonlinearity = 0
  MatrixSolverType = 0
  SplitInputWriter = false
  ThermoMechSteadyState = true
  TimeEnd = 1
  TimeInitialStep = 1
